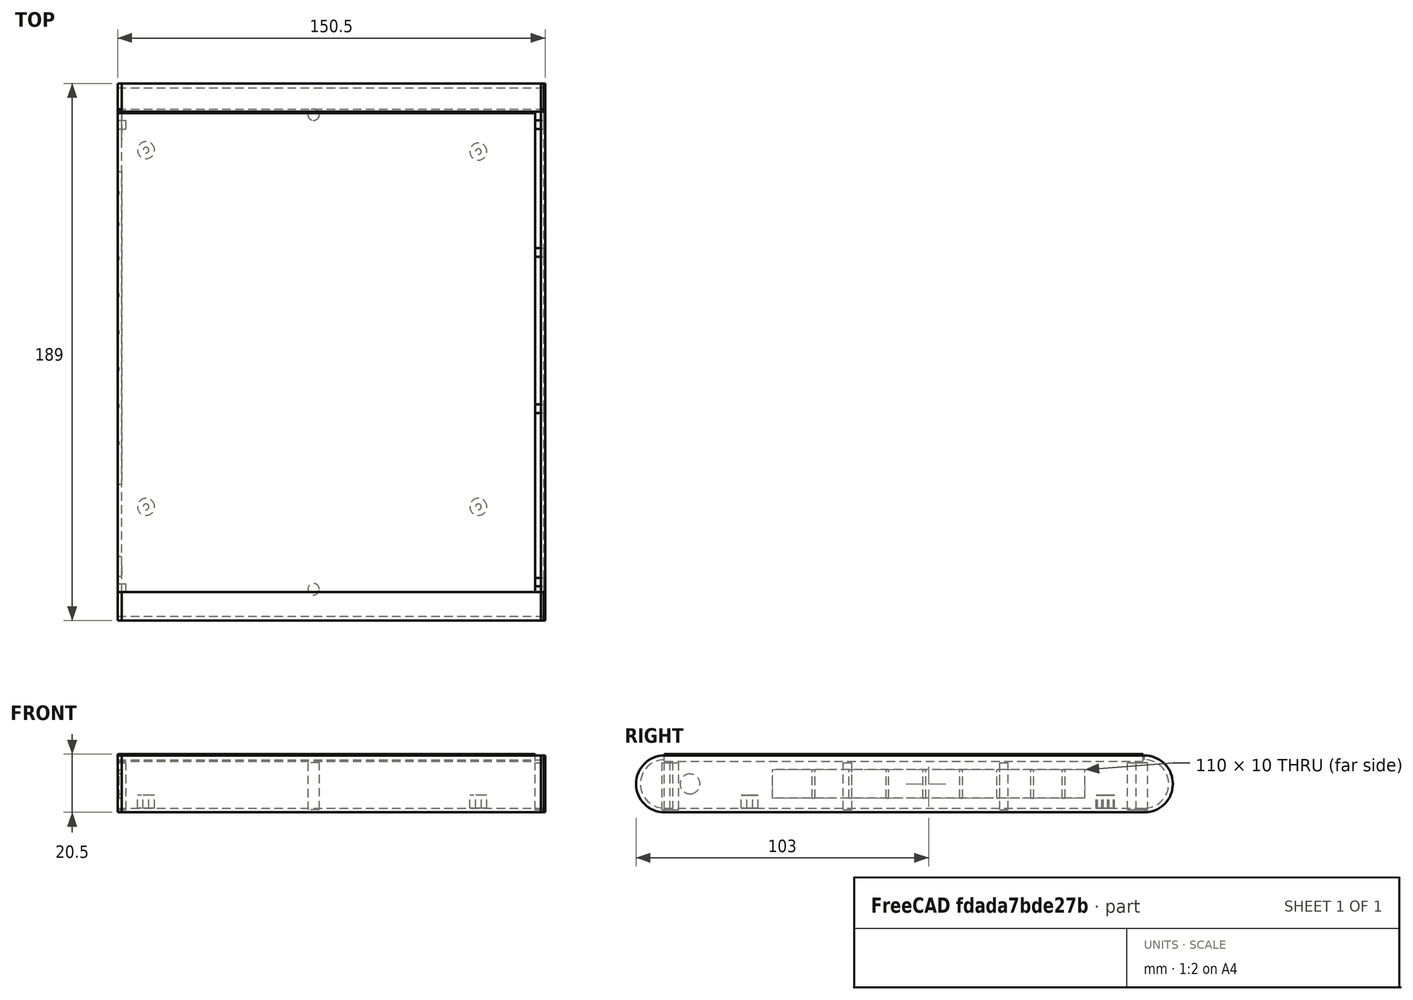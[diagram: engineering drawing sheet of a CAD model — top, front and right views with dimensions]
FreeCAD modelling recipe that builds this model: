
FCSTD DOCUMENT  (FreeCAD 0.20R29603 (Git))
Label: case2
License: All rights reserved
LicenseURL: http://en.wikipedia.org/wiki/All_rights_reserved
objects: Part::Box×20, Part::Cylinder×7, Part::FeaturePython×6, Part::MultiFuse×5, Part::Cut×3, App::DocumentObjectGroup×2
note: 41 computed .brp shape members not serialized (recipe doc carries the construction recipe); baked Part::Feature solids carry a one-line shape summary decoded from their .brp

FEATURE [Part::Box] Box  label="base"
  AttacherType = Attacher::AttachEngine3D
  Height = 1.5
  Length = 150
  Placement = pos=(0,0,-10) rot=(1,0,0;0rad)
  Width = 170
FEATURE [Part::FeaturePython] Tube  label="LeftCurve"  # WARN: FeaturePython — macro-defined, semantics opaque (R4)
  AttacherType = Attacher::AttachEngine3D
  Height = 150
  InnerRadius = 8.5
  OuterRadius = 10
  Placement = pos=(0,0,0) rot=(0,1,0;1.5708rad)
FEATURE [Part::FeaturePython] Tube001  label="RightCurve"  # WARN: FeaturePython — macro-defined, semantics opaque (R4)
  AttacherType = Attacher::AttachEngine3D
  Height = 150
  InnerRadius = 8.5
  OuterRadius = 10
  Placement = pos=(0,169,0) rot=(0,1,0;1.5708rad)
FEATURE [Part::Cylinder] Cylinder
  Angle = 360
  AttacherType = Attacher::AttachEngine3D
  FirstAngle = 0
  Height = 1.5
  Placement = pos=(0,0,0) rot=(0,1,0;1.5708rad)
  Radius = 10
  SecondAngle = 0
FEATURE [Part::Cylinder] Cylinder001
  Angle = 360
  AttacherType = Attacher::AttachEngine3D
  FirstAngle = 0
  Height = 1.5
  Placement = pos=(0,169,0) rot=(0,1,0;1.5708rad)
  Radius = 10
  SecondAngle = 0
FEATURE [Part::Box] Box001  label="Cube001"
  AttacherType = Attacher::AttachEngine3D
  Height = 20
  Length = 1.5
  Placement = pos=(0,0,-10) rot=(0,0,1;0rad)
  Width = 170
FEATURE [Part::MultiFuse] Fusion  label="Front"
  Placement = pos=(149,0,0) rot=(0,0,1;0rad)
  Shapes = -> [Cylinder,Cylinder001,Box001]
FEATURE [Part::Box] Box002  label="Cube002"
  AttacherType = Attacher::AttachEngine3D
  Height = 20
  Length = 1.5
  Placement = pos=(0,0,-10) rot=(0,0,1;0rad)
  Width = 170
FEATURE [Part::Cylinder] Cylinder002
  Angle = 360
  AttacherType = Attacher::AttachEngine3D
  FirstAngle = 0
  Height = 1.5
  Placement = pos=(0,0,0) rot=(0,1,0;1.5708rad)
  Radius = 10
  SecondAngle = 0
FEATURE [Part::Cylinder] Cylinder003
  Angle = 360
  AttacherType = Attacher::AttachEngine3D
  FirstAngle = 0
  Height = 1.5
  Placement = pos=(0,169,0) rot=(0,1,0;1.5708rad)
  Radius = 10
  SecondAngle = 0
FEATURE [Part::MultiFuse] Fusion001  label="back"
  Shapes = -> [Cylinder002,Cylinder003,Box002]
FEATURE [Part::MultiFuse] Fusion002  label="Sides"
  Shapes = -> [Tube,Tube001]
FEATURE [Part::Box] Box003  label="Cube"
  AttacherType = Attacher::AttachEngine3D
  Height = 22
  Length = 150
  Placement = pos=(0,0,-11) rot=(0,0,1;0rad)
  Width = 169
FEATURE [Part::Cut] Cut
  Base = -> Fusion002
  Tool = -> Box003
FEATURE [Part::FeaturePython] Tube002  # WARN: FeaturePython — macro-defined, semantics opaque (R4)
  AttacherType = Attacher::AttachEngine3D
  Height = 5
  InnerRadius = 1
  OuterRadius = 3
  Placement = pos=(10,10,-9) rot=(0,0,1;0rad)
FEATURE [Part::FeaturePython] Tube003  # WARN: FeaturePython — macro-defined, semantics opaque (R4)
  AttacherType = Attacher::AttachEngine3D
  Height = 5
  InnerRadius = 1
  OuterRadius = 3
  Placement = pos=(10,135.5,-9) rot=(0,0,1;0rad)
FEATURE [Part::FeaturePython] Tube004  # WARN: FeaturePython — macro-defined, semantics opaque (R4)
  AttacherType = Attacher::AttachEngine3D
  Height = 5
  InnerRadius = 1
  OuterRadius = 3
  Placement = pos=(127,135,-9) rot=(0,0,1;0rad)
FEATURE [Part::FeaturePython] Tube005  # WARN: FeaturePython — macro-defined, semantics opaque (R4)
  AttacherType = Attacher::AttachEngine3D
  Height = 5
  InnerRadius = 1
  OuterRadius = 3
  Placement = pos=(127,10,-9) rot=(0,0,1;0rad)
FEATURE [Part::Box] Box004  label="Cube003"
  AttacherType = Attacher::AttachEngine3D
  Height = 10
  Length = 10
  Placement = pos=(-3,38,-5) rot=(0,0,1;0rad)
  Width = 110
FEATURE [Part::Box] Box005  label="top"
  AttacherType = Attacher::AttachEngine3D
  Height = 2.5
  Length = 147
  Placement = pos=(0,0,8) rot=(1,0,0;0rad)
  Width = 168.5
FEATURE [Part::Cut] Cut001
  Base = -> Fusion001
  Tool = -> Box004
FEATURE [Part::MultiFuse] Fusion003
  Placement = pos=(0,20,0) rot=(0,0,1;0rad)
  Shapes = -> [Tube002,Tube003,Tube004,Tube005]
FEATURE [Part::Cylinder] Cylinder004  label="pwrjack"
  Angle = 360
  AttacherType = Attacher::AttachEngine3D
  FirstAngle = 0
  Height = 10
  Placement = pos=(-3,9,0) rot=(0,1,0;1.5708rad)
  Radius = 3.5
  SecondAngle = 0
FEATURE [Part::Cut] Cut003
  Base = -> Cut001
  Tool = -> Cylinder004
FEATURE [Part::Box] Box006  label="Cube004"
  AttacherType = Attacher::AttachEngine3D
  Height = 16.5
  Length = 3
  Placement = pos=(0,0,-9) rot=(0,0,1;0rad)
  Width = 3
FEATURE [Part::Box] Box007  label="Cube005"
  AttacherType = Attacher::AttachEngine3D
  Height = 16.5
  Length = 3
  Placement = pos=(0,163,-9) rot=(0,0,1;0rad)
  Width = 3
FEATURE [Part::Box] Box008  label="Cube006"
  AttacherType = Attacher::AttachEngine3D
  Height = 16.5
  Length = 3
  Placement = pos=(147,118,-9) rot=(0,0,1;0rad)
  Width = 3
FEATURE [Part::Box] Box009  label="Cube007"
  AttacherType = Attacher::AttachEngine3D
  Height = 16.5
  Length = 3
  Placement = pos=(147,163,-9) rot=(0,0,1;0rad)
  Width = 3
FEATURE [Part::Box] Box010  label="Cube008"
  AttacherType = Attacher::AttachEngine3D
  Height = 16.5
  Length = 3
  Placement = pos=(147,63,-9) rot=(0,0,1;0rad)
  Width = 3
FEATURE [Part::Box] Box011  label="Cube009"
  AttacherType = Attacher::AttachEngine3D
  Height = 16.5
  Length = 3
  Placement = pos=(147,2,-9) rot=(0,0,1;0rad)
  Width = 3
FEATURE [Part::Cylinder] Cylinder005
  Angle = 360
  AttacherType = Attacher::AttachEngine3D
  FirstAngle = 0
  Height = 16.5
  Placement = pos=(69,1,-9) rot=(0,0,1;0rad)
  Radius = 2
  SecondAngle = 0
FEATURE [Part::Cylinder] Cylinder006
  Angle = 360
  AttacherType = Attacher::AttachEngine3D
  FirstAngle = 0
  Height = 16.5
  Placement = pos=(69,168,-9) rot=(0,0,1;0rad)
  Radius = 2
  SecondAngle = 0
FEATURE [App::DocumentObjectGroup] Group001  label="CaseTop"
  Group = -> [Box005]
FEATURE [Part::Box] Box012  label="Cube010"
  AttacherType = Attacher::AttachEngine3D
  Height = 10
  Length = 0.5
  Placement = pos=(0,65,-5) rot=(0,0,1;0rad)
  Width = 1
FEATURE [Part::Box] Box013  label="Cube011"
  AttacherType = Attacher::AttachEngine3D
  Height = 10
  Length = 0.5
  Placement = pos=(0,52,-5) rot=(0,0,1;0rad)
  Width = 1
FEATURE [Part::Box] Box014  label="Cube012"
  AttacherType = Attacher::AttachEngine3D
  Height = 10
  Length = 0.5
  Placement = pos=(0,78,-5) rot=(0,0,1;0rad)
  Width = 1
FEATURE [Part::Box] Box015  label="Cube013"
  AttacherType = Attacher::AttachEngine3D
  Height = 10
  Length = 0.5
  Placement = pos=(0,91,-5) rot=(0,0,1;0rad)
  Width = 1
FEATURE [Part::Box] Box016  label="Cube014"
  AttacherType = Attacher::AttachEngine3D
  Height = 10
  Length = 0.5
  Placement = pos=(0,104,-5) rot=(0,0,1;0rad)
  Width = 1
FEATURE [Part::Box] Box017  label="Cube015"
  AttacherType = Attacher::AttachEngine3D
  Height = 10
  Length = 0.5
  Placement = pos=(0,117,-5) rot=(0,0,1;0rad)
  Width = 1
FEATURE [Part::Box] Box018  label="Cube016"
  AttacherType = Attacher::AttachEngine3D
  Height = 10
  Length = 0.5
  Placement = pos=(0,129,-5) rot=(0,0,1;0rad)
  Width = 1
FEATURE [Part::Box] Box019  label="Cube017"
  AttacherType = Attacher::AttachEngine3D
  Height = 10
  Length = 0.5
  Placement = pos=(0,140,-5) rot=(0,0,1;0rad)
  Width = 1
FEATURE [Part::MultiFuse] Fusion004
  Shapes = -> [Fusion003,Box]
FEATURE [App::DocumentObjectGroup] Group  label="CaseBase"
  Group = -> [Fusion,Cut,Cut003,Box006,Box007,Box008,Box009,Box010,Box011,Cylinder005,Cylinder006,Box012,Box013,Box014,Box015,Box016,Box017,Box018,Box019,Fusion004]
